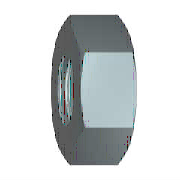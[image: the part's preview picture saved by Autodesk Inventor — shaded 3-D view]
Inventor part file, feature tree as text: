
AUTODESK INVENTOR PART (.ipt)
format: ipt  version: 2015 (Build 190159000, 159)  size: 161,280 bytes
history: native  units: mm (DEFAULTED — no unit token found)
features: sketch x3, chamfer x1, hole x1, other x1, plane x1
ambient origin geometry x7: Origin, YZ Plane, XZ Plane, X Axis, Y Axis, Z Axis, Center Point
bodies: Solid1 (feature_tree), Body (feature_tree)
feature tree (7):
  chamfer  "Chamfer1"  Angle=30.0deg  [1 undecoded]
  hole  "Thread"  [1 undecoded]
  other  "Work Axis1"
  plane  "Work Plane1"
  sketch  "Sketch1"  dims[d0=6.350853mm]
  sketch  "Sketch2"  dims[d1=2.4mm]
  sketch  "Sketch3"  dims[d2=0.0mm d3=30.0deg d4=30.0deg d5=4.5mm d6=4.5mm d7=90.0deg d25=2.459mm d26=6.0mm d27=4.0mm d28=2.0mm d29=14.3117mm d30=8.0mm d31=20.594885mm d8=0.270633mm d9=30.0deg d10=0.270633mm d11=30.0deg d13=0.0mm d14=0.0mm d39=0.0mm d40=0.270633mm d41=0.270633mm d42=0.0mm]
note: 2 required parameter values undecoded (feature->parameter linkage not recoverable at this tier; creation-order binding heuristic only, values carry confidence <= 0.55)
